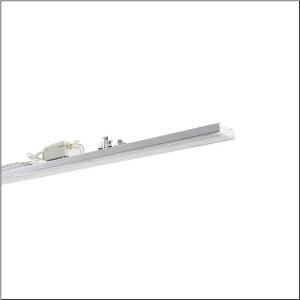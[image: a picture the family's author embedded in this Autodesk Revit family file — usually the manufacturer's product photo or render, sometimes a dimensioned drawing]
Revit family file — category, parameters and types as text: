
# Revit family: licross_21_recessed_mo_52tl197n48xg
name_source: partatom
category: Lighting Fixtures
units: mm (PartAtom-declared; Revit-internal decimal feet)

## family parameters
Cut with Voids When Loaded = No
Host = Face
Light Source = No
Part Type = Normal
Room Calculation Point = No
Round Connector Dimension = Use Diameter
Shared = No

## types (1)
- Licross 21 Recessed MO (1 x LED, 8450 lm, 47.9 W, 4000K)
    Apparent Load = 48 VA
    CIE Flux Codes = 55 90 98 100 100
    Color Rendering = 80
    Color Temperature = 4000K
    Default Elevation = 1800 mm
    Description = Licross 21 Recessed MO, luminaire insert, of sheet steel, galvanised, coil coated, white, length: 1.500mm, width: 66mm, height: 67mm, LED rated luminous flux: 8.450lm, light colour: 840, SDCM (Standard Deviation of Colour Matching)MacAdam ≤ 3 SDCM (initial), control gear: ON/OFF, with plug, 3-pole, with phase selection, mains connection: 220..240V, AC, 50/60Hz, rated input power: 48W, internal wiring halogen-free, primary light control with lens, of plastic, primary optical cover: cover, of PMMA, light emission: direct distribution, primary light characteristic: double asymmetric, protection rating (complete): IP40, insulation class (complete): insulation class I (protective earthing), certification: CE, ENEC, VDE, UKCA, protection symbol: D if used in an environment without relevant dust loads with corresponding accessories, impact resistance: IK06, permissible ambient temperature for indoor applications: -35..+40°C, corresponds to IFS (International Featured Standards) requirements for safety and quality in the food industry, reducing of maximum allowable ambient temperature of 5°C with ceiling mounting, LABS conformity tested according to VDMA 24364:2018-05, The light source and the operating device comply with the requirements of the Ecodesign Regulation (EU) 2019/2020 and are replaceable in accordance with this regulation, packaging unit: 1 piece
    Height = 58 mm
    Lamp = 1 x LED
    Lamp Light Flux = 8450 lm
    Lamp Power = 47.9 W
    Lamp count = 1
    Length = 1500 mm
    Luminous efficacy = 176 lm/W
    Manufacturer = Siteco
    ModVariant = No
    Model = 52TL197N48XG
    Mounting Place = Ceiling
    Mounting Type = Pendant
    Number of Poles = 1
    OnlyDefault = Yes
    Power Factor = 1
    Product Name = Licross 21 Recessed MO
    Product group = luminaire insert | ceiling pendant
    ProductGroupID = 901
    Protection Class = Protection class I
    Protection Degree = IP 40
    RLX_Detail_Level = 1
    RLX_Emergency_Light_Flux = 0 lm
    RLX_Emergency_Type = 0
    RLX_Emergency_Type_DB = No
    RlxData = <blob elided: 21177 chars, md5=12cea893>
    Socket = socket
    Standby Power = 0 W
    System Light Flux = 8450 lm
    System Power = 48 W
    Type Comments = Product without accessories
    Type Image = l_1296930.jpg
    URL = http://relux.com
    VarID = ---
    Voltage = 0 V
    Weight = 0.00 kg
    Width = 66 mm

## geometry (parser evidence)
native form markers: Blend x4, Sweep x9
no freeform markers — native parametric forms only
